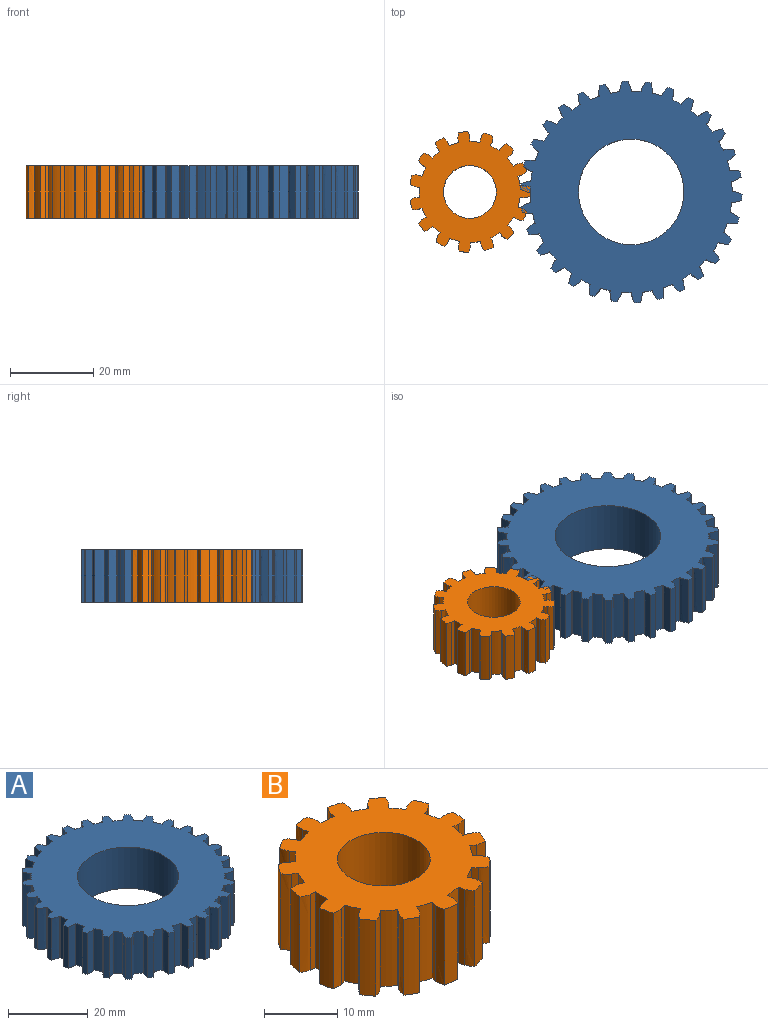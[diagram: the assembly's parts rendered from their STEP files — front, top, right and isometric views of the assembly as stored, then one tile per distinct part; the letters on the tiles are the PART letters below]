
ASSEMBLY  parts=2 mates=1
PART A: 183 faces, bbox 53.4x53.4x12.7 mm
  f0: cylinder r=24.29mm len=12.7mm, axis (0,0,-1), area 30.3mm2, adj f32,f34,f35,f147
  f1: cylinder r=24.29mm len=12.7mm, axis (0,0,-1), area 30.3mm2, adj f34,f35,f142,f146
  f2: cylinder r=24.29mm len=12.7mm, axis (0,0,-1), area 30.3mm2, adj f34,f35,f137,f141
  f3: cylinder r=24.29mm len=12.7mm, axis (0,0,-1), area 30.3mm2, adj f34,f35,f132,f136
  f4: cylinder r=24.29mm len=12.7mm, axis (0,0,-1), area 30.3mm2, adj f34,f35,f127,f131
  f5: cylinder r=24.29mm len=12.7mm, axis (0,0,-1), area 30.3mm2, adj f34,f35,f122,f126
  f6: cylinder r=24.29mm len=12.7mm, axis (0,0,-1), area 30.3mm2, adj f34,f35,f117,f121
  f7: cylinder r=24.29mm len=12.7mm, axis (0,0,-1), area 30.3mm2, adj f34,f35,f112,f116
  f8: cylinder r=24.29mm len=12.7mm, axis (0,0,-1), area 30.3mm2, adj f34,f35,f107,f111
  f9: cylinder r=24.29mm len=12.7mm, axis (0,0,-1), area 30.3mm2, adj f34,f35,f102,f106
  f10: cylinder r=24.29mm len=12.7mm, axis (0,0,-1), area 30.3mm2, adj f34,f35,f97,f101
  f11: cylinder r=24.29mm len=12.7mm, axis (0,0,-1), area 30.3mm2, adj f34,f35,f92,f96
  f12: cylinder r=24.29mm len=12.7mm, axis (0,0,-1), area 30.3mm2, adj f34,f35,f87,f91
  f13: cylinder r=24.29mm len=12.7mm, axis (0,0,-1), area 30.3mm2, adj f34,f35,f82,f86
  f14: cylinder r=24.29mm len=12.7mm, axis (0,0,-1), area 30.3mm2, adj f34,f35,f77,f81
  f15: cylinder r=24.29mm len=12.7mm, axis (0,0,-1), area 30.3mm2, adj f34,f35,f72,f76
  f16: cylinder r=24.29mm len=12.7mm, axis (0,0,-1), area 30.3mm2, adj f34,f35,f67,f71
  f17: cylinder r=24.29mm len=12.7mm, axis (0,0,-1), area 30.3mm2, adj f34,f35,f62,f66
  f18: cylinder r=24.29mm len=12.7mm, axis (0,0,-1), area 30.3mm2, adj f34,f35,f57,f61
  f19: cylinder r=24.29mm len=12.7mm, axis (0,0,-1), area 30.3mm2, adj f34,f35,f52,f56
  f20: cylinder r=24.29mm len=12.7mm, axis (0,0,-1), area 30.3mm2, adj f34,f35,f47,f51
  f21: cylinder r=24.29mm len=12.7mm, axis (0,0,-1), area 30.3mm2, adj f34,f35,f42,f46
  f22: cylinder r=24.29mm len=12.7mm, axis (0,0,-1), area 30.3mm2, adj f34,f35,f41,f182
  f23: cylinder r=24.29mm len=12.7mm, axis (0,0,-1), area 30.3mm2, adj f34,f35,f177,f181
  f24: cylinder r=24.29mm len=12.7mm, axis (0,0,-1), area 30.3mm2, adj f34,f35,f172,f176
  f25: cylinder r=24.29mm len=12.7mm, axis (0,0,-1), area 30.3mm2, adj f34,f35,f167,f171
  f26: cylinder r=24.29mm len=12.7mm, axis (0,0,-1), area 30.3mm2, adj f34,f35,f162,f166
  f27: cylinder r=24.29mm len=12.7mm, axis (0,0,-1), area 30.3mm2, adj f34,f35,f157,f161
  f28: cylinder r=24.29mm len=12.7mm, axis (0,0,-1), area 30.3mm2, adj f34,f35,f151,f156
  f29: extruded ~12.7x2.16mm, area 29.2mm2, adj f30,f33,f34,f35
  f30: cylinder r=26.67mm len=12.7mm, axis (0,0,-1), area 18.2mm2, adj f29,f31,f34,f35
  f31: extruded ~12.7x2.23mm, area 29.2mm2, adj f30,f32,f34,f35
  f32: plane 12.7x0.21mm, normal (-0.99,-0.11,0), area 2.7mm2, adj f0,f31,f34,f35
  f33: plane 12.7x0.21mm, normal (1,0,0), area 2.7mm2, adj f29,f34,f35,f37
  f34: plane 53.37x53.36mm, normal (0,0,1), area 1505.3mm2, adj f0,f1,f2,f3,f4,f5,f6,f7
  f35: plane 53.37x53.36mm, normal (0,0,-1), area 1505.3mm2, adj f0,f1,f2,f3,f4,f5,f6,f7
  f36: cylinder r=12.7mm len=25.4mm, axis (0,0,-1), area 1013.4mm2, adj f34,f35
  f37: cylinder r=24.29mm len=12.7mm, axis (0,0,-1), area 30.3mm2, adj f33,f34,f35,f152
  f38: extruded ~12.7x2.23mm, area 29.2mm2, adj f34,f35,f39,f42
  f39: cylinder r=26.67mm len=12.7mm, axis (0,0,-1), area 18.2mm2, adj f34,f35,f38,f40
  f40: extruded ~12.7x2.17mm, area 29.2mm2, adj f34,f35,f39,f41
  f41: plane 12.7x0.21mm, normal (-0.01,1,0), area 2.7mm2, adj f22,f34,f35,f40
  f42: plane 12.7x0.21mm, normal (-0.1,-0.99,0), area 2.7mm2, adj f21,f34,f35,f38
  f43: extruded ~12.7x2.29mm, area 29.2mm2, adj f34,f35,f44,f47
  f44: cylinder r=26.67mm len=12.7mm, axis (0,0,-1), area 18.2mm2, adj f34,f35,f43,f45
  f45: extruded ~12.7x1.96mm, area 29.2mm2, adj f34,f35,f44,f46
  f46: plane 12.7x0.21mm, normal (0.2,0.98,0), area 2.7mm2, adj f21,f34,f35,f45
  f47: plane 12.7x0.2mm, normal (-0.31,-0.95,0), area 2.7mm2, adj f20,f34,f35,f43
  f48: extruded ~12.7x2.25mm, area 29.2mm2, adj f34,f35,f49,f52
  f49: cylinder r=26.67mm len=12.7mm, axis (0,0,-1), area 18.2mm2, adj f34,f35,f48,f50
  f50: extruded ~12.7x1.67mm, area 29.2mm2, adj f34,f35,f49,f51
  f51: plane 12.7x0.19mm, normal (0.4,0.92,0), area 2.7mm2, adj f20,f34,f35,f50
  f52: plane 12.7x0.18mm, normal (-0.5,-0.87,0), area 2.7mm2, adj f19,f34,f35,f48
  f53: extruded ~12.7x2.12mm, area 29.2mm2, adj f34,f35,f54,f57
  f54: cylinder r=26.67mm len=12.7mm, axis (0,0,-1), area 18.2mm2, adj f34,f35,f53,f55
  f55: extruded ~12.7x1.88mm, area 29.2mm2, adj f34,f35,f54,f56
  f56: plane 12.7x0.17mm, normal (0.58,0.81,0), area 2.7mm2, adj f19,f34,f35,f55
  f57: plane 12.7x0.16mm, normal (-0.67,-0.74,0), area 2.7mm2, adj f18,f34,f35,f53
  f58: extruded ~12.7x1.89mm, area 29.2mm2, adj f34,f35,f59,f62
  f59: cylinder r=26.67mm len=12.7mm, axis (0,0,-1), area 18.2mm2, adj f34,f35,f58,f60
  f60: extruded ~12.7x2.11mm, area 29.2mm2, adj f34,f35,f59,f61
  f61: plane 12.7x0.15mm, normal (0.74,0.67,0), area 2.7mm2, adj f18,f34,f35,f60
  f62: plane 12.7x0.17mm, normal (-0.81,-0.59,0), area 2.7mm2, adj f17,f34,f35,f58
  f63: extruded ~12.7x1.66mm, area 29.2mm2, adj f34,f35,f64,f67
  f64: cylinder r=26.67mm len=12.7mm, axis (0,0,-1), area 18.2mm2, adj f34,f35,f63,f65
  f65: extruded ~12.7x2.25mm, area 29.2mm2, adj f34,f35,f64,f66
  f66: plane 12.7x0.18mm, normal (0.86,0.51,0), area 2.7mm2, adj f17,f34,f35,f65
  f67: plane 12.7x0.19mm, normal (-0.91,-0.41,0), area 2.7mm2, adj f16,f34,f35,f63
  f68: extruded ~12.7x1.95mm, area 29.2mm2, adj f34,f35,f69,f72
  f69: cylinder r=26.67mm len=12.7mm, axis (0,0,-1), area 18.2mm2, adj f34,f35,f68,f70
  f70: extruded ~12.7x2.29mm, area 29.2mm2, adj f34,f35,f69,f71
  f71: plane 12.7x0.2mm, normal (0.95,0.32,0), area 2.7mm2, adj f16,f34,f35,f70
  f72: plane 12.7x0.21mm, normal (-0.98,-0.21,0), area 2.7mm2, adj f15,f34,f35,f68
  f73: extruded ~12.7x2.16mm, area 29.2mm2, adj f34,f35,f74,f77
  f74: cylinder r=26.67mm len=12.7mm, axis (0,0,-1), area 18.2mm2, adj f34,f35,f73,f75
  f75: extruded ~12.7x2.23mm, area 29.2mm2, adj f34,f35,f74,f76
  f76: plane 12.7x0.21mm, normal (0.99,0.11,0), area 2.7mm2, adj f15,f34,f35,f75
  f77: plane 12.7x0.21mm, normal (-1,0,0), area 2.7mm2, adj f14,f34,f35,f73
  f78: extruded ~12.7x2.27mm, area 29.2mm2, adj f34,f35,f79,f82
  f79: cylinder r=26.67mm len=12.7mm, axis (0,0,-1), area 18.2mm2, adj f34,f35,f78,f80
  f80: extruded ~12.7x2.08mm, area 29.2mm2, adj f34,f35,f79,f81
  f81: plane 12.7x0.21mm, normal (1,-0.1,0), area 2.7mm2, adj f14,f34,f35,f80
  f82: plane 12.7x0.21mm, normal (-0.98,0.21,0), area 2.7mm2, adj f13,f34,f35,f78
  f83: extruded ~12.7x2.29mm, area 29.2mm2, adj f34,f35,f84,f87
  f84: cylinder r=26.67mm len=12.7mm, axis (0,0,-1), area 18.2mm2, adj f34,f35,f83,f85
  f85: extruded ~12.7x1.83mm, area 29.2mm2, adj f34,f35,f84,f86
  f86: plane 12.7x0.2mm, normal (0.95,-0.3,0), area 2.7mm2, adj f13,f34,f35,f85
  f87: plane 12.7x0.19mm, normal (-0.91,0.41,0), area 2.7mm2, adj f12,f34,f35,f83
  f88: extruded ~12.7x2.2mm, area 29.2mm2, adj f34,f35,f89,f92
  f89: cylinder r=26.67mm len=12.7mm, axis (0,0,-1), area 18.2mm2, adj f34,f35,f88,f90
  f90: extruded ~12.7x1.73mm, area 29.2mm2, adj f34,f35,f89,f91
  f91: plane 12.7x0.18mm, normal (0.87,-0.49,0), area 2.7mm2, adj f12,f34,f35,f90
  f92: plane 12.7x0.17mm, normal (-0.81,0.59,0), area 2.7mm2, adj f11,f34,f35,f88
  f93: extruded ~12.7x2.02mm, area 29.2mm2, adj f34,f35,f94,f97
  f94: cylinder r=26.67mm len=12.7mm, axis (0,0,-1), area 18.2mm2, adj f34,f35,f93,f95
  f95: extruded ~12.7x2.01mm, area 29.2mm2, adj f34,f35,f94,f96
  f96: plane 12.7x0.16mm, normal (0.75,-0.66,0), area 2.7mm2, adj f11,f34,f35,f95
  f97: plane 12.7x0.16mm, normal (-0.67,0.74,0), area 2.7mm2, adj f10,f34,f35,f93
  f98: extruded ~12.7x1.74mm, area 29.2mm2, adj f34,f35,f99,f102
  f99: cylinder r=26.67mm len=12.7mm, axis (0,0,-1), area 18.2mm2, adj f34,f35,f98,f100
  f100: extruded ~12.7x2.19mm, area 29.2mm2, adj f34,f35,f99,f101
  f101: plane 12.7x0.17mm, normal (0.59,-0.81,0), area 2.7mm2, adj f10,f34,f35,f100
  f102: plane 12.7x0.18mm, normal (-0.5,0.87,0), area 2.7mm2, adj f9,f34,f35,f98
  f103: extruded ~12.7x1.82mm, area 29.2mm2, adj f34,f35,f104,f107
  f104: cylinder r=26.67mm len=12.7mm, axis (0,0,-1), area 18.2mm2, adj f34,f35,f103,f105
  f105: extruded ~12.7x2.28mm, area 29.2mm2, adj f34,f35,f104,f106
  f106: plane 12.7x0.19mm, normal (0.41,-0.91,0), area 2.7mm2, adj f9,f34,f35,f105
  f107: plane 12.7x0.2mm, normal (-0.31,0.95,0), area 2.7mm2, adj f8,f34,f35,f103
  f108: extruded ~12.7x2.07mm, area 29.2mm2, adj f34,f35,f109,f112
  f109: cylinder r=26.67mm len=12.7mm, axis (0,0,-1), area 18.2mm2, adj f34,f35,f108,f110
  f110: extruded ~12.7x2.28mm, area 29.2mm2, adj f34,f35,f109,f111
  f111: plane 12.7x0.2mm, normal (0.21,-0.98,0), area 2.7mm2, adj f8,f34,f35,f110
  f112: plane 12.7x0.21mm, normal (-0.1,0.99,0), area 2.7mm2, adj f7,f34,f35,f108
  f113: extruded ~12.7x2.23mm, area 29.2mm2, adj f34,f35,f114,f117
  f114: cylinder r=26.67mm len=12.7mm, axis (0,0,-1), area 18.2mm2, adj f34,f35,f113,f115
  f115: extruded ~12.7x2.17mm, area 29.2mm2, adj f34,f35,f114,f116
  f116: plane 12.7x0.21mm, normal (0.01,-1,0), area 2.7mm2, adj f7,f34,f35,f115
  f117: plane 12.7x0.21mm, normal (0.1,0.99,0), area 2.7mm2, adj f6,f34,f35,f113
  f118: extruded ~12.7x2.29mm, area 29.2mm2, adj f34,f35,f119,f122
  f119: cylinder r=26.67mm len=12.7mm, axis (0,0,-1), area 18.2mm2, adj f34,f35,f118,f120
  f120: extruded ~12.7x1.96mm, area 29.2mm2, adj f34,f35,f119,f121
  f121: plane 12.7x0.21mm, normal (-0.2,-0.98,0), area 2.7mm2, adj f6,f34,f35,f120
  f122: plane 12.7x0.2mm, normal (0.31,0.95,0), area 2.7mm2, adj f5,f34,f35,f118
  f123: extruded ~12.7x2.25mm, area 29.2mm2, adj f34,f35,f124,f127
  f124: cylinder r=26.67mm len=12.7mm, axis (0,0,-1), area 18.2mm2, adj f34,f35,f123,f125
  f125: extruded ~12.7x1.67mm, area 29.2mm2, adj f34,f35,f124,f126
  f126: plane 12.7x0.19mm, normal (-0.4,-0.92,0), area 2.7mm2, adj f5,f34,f35,f125
  f127: plane 12.7x0.18mm, normal (0.5,0.87,0), area 2.7mm2, adj f4,f34,f35,f123
  f128: extruded ~12.7x2.12mm, area 29.2mm2, adj f34,f35,f129,f132
  f129: cylinder r=26.67mm len=12.7mm, axis (0,0,-1), area 18.2mm2, adj f34,f35,f128,f130
  f130: extruded ~12.7x1.88mm, area 29.2mm2, adj f34,f35,f129,f131
  f131: plane 12.7x0.17mm, normal (-0.58,-0.81,0), area 2.7mm2, adj f4,f34,f35,f130
  f132: plane 12.7x0.16mm, normal (0.67,0.74,0), area 2.7mm2, adj f3,f34,f35,f128
  f133: extruded ~12.7x1.89mm, area 29.2mm2, adj f34,f35,f134,f137
  f134: cylinder r=26.67mm len=12.7mm, axis (0,0,-1), area 18.2mm2, adj f34,f35,f133,f135
  f135: extruded ~12.7x2.11mm, area 29.2mm2, adj f34,f35,f134,f136
  f136: plane 12.7x0.15mm, normal (-0.74,-0.67,0), area 2.7mm2, adj f3,f34,f35,f135
  f137: plane 12.7x0.17mm, normal (0.81,0.59,0), area 2.7mm2, adj f2,f34,f35,f133
  f138: extruded ~12.7x1.66mm, area 29.2mm2, adj f34,f35,f139,f142
  f139: cylinder r=26.67mm len=12.7mm, axis (0,0,-1), area 18.2mm2, adj f34,f35,f138,f140
  f140: extruded ~12.7x2.25mm, area 29.2mm2, adj f34,f35,f139,f141
  f141: plane 12.7x0.18mm, normal (-0.86,-0.51,0), area 2.7mm2, adj f2,f34,f35,f140
  f142: plane 12.7x0.19mm, normal (0.91,0.41,0), area 2.7mm2, adj f1,f34,f35,f138
  f143: extruded ~12.7x1.95mm, area 29.2mm2, adj f34,f35,f144,f147
  f144: cylinder r=26.67mm len=12.7mm, axis (0,0,-1), area 18.2mm2, adj f34,f35,f143,f145
  f145: extruded ~12.7x2.29mm, area 29.2mm2, adj f34,f35,f144,f146
  f146: plane 12.7x0.2mm, normal (-0.95,-0.32,0), area 2.7mm2, adj f1,f34,f35,f145
  f147: plane 12.7x0.21mm, normal (0.98,0.21,0), area 2.7mm2, adj f0,f34,f35,f143
  f148: extruded ~12.7x2.27mm, area 29.2mm2, adj f34,f35,f149,f151
  f149: cylinder r=26.67mm len=12.7mm, axis (0,0,-1), area 18.2mm2, adj f34,f35,f148,f150
  f150: extruded ~12.7x2.08mm, area 29.2mm2, adj f34,f35,f149,f152
  f151: plane 12.7x0.21mm, normal (0.98,-0.21,0), area 2.7mm2, adj f28,f34,f35,f148
  f152: plane 12.7x0.21mm, normal (-1,0.1,0), area 2.7mm2, adj f34,f35,f37,f150
  f153: extruded ~12.7x2.29mm, area 29.2mm2, adj f34,f35,f154,f157
  f154: cylinder r=26.67mm len=12.7mm, axis (0,0,-1), area 18.2mm2, adj f34,f35,f153,f155
  f155: extruded ~12.7x1.83mm, area 29.2mm2, adj f34,f35,f154,f156
  f156: plane 12.7x0.2mm, normal (-0.95,0.3,0), area 2.7mm2, adj f28,f34,f35,f155
  f157: plane 12.7x0.19mm, normal (0.91,-0.41,0), area 2.7mm2, adj f27,f34,f35,f153
  f158: extruded ~12.7x2.2mm, area 29.2mm2, adj f34,f35,f159,f162
  f159: cylinder r=26.67mm len=12.7mm, axis (0,0,-1), area 18.2mm2, adj f34,f35,f158,f160
  f160: extruded ~12.7x1.73mm, area 29.2mm2, adj f34,f35,f159,f161
  f161: plane 12.7x0.18mm, normal (-0.87,0.49,0), area 2.7mm2, adj f27,f34,f35,f160
  f162: plane 12.7x0.17mm, normal (0.81,-0.59,0), area 2.7mm2, adj f26,f34,f35,f158
  f163: extruded ~12.7x2.02mm, area 29.2mm2, adj f34,f35,f164,f167
  f164: cylinder r=26.67mm len=12.7mm, axis (0,0,-1), area 18.2mm2, adj f34,f35,f163,f165
  f165: extruded ~12.7x2.01mm, area 29.2mm2, adj f34,f35,f164,f166
  f166: plane 12.7x0.16mm, normal (-0.75,0.66,0), area 2.7mm2, adj f26,f34,f35,f165
  f167: plane 12.7x0.16mm, normal (0.67,-0.74,0), area 2.7mm2, adj f25,f34,f35,f163
  f168: extruded ~12.7x1.74mm, area 29.2mm2, adj f34,f35,f169,f172
  f169: cylinder r=26.67mm len=12.7mm, axis (0,0,-1), area 18.2mm2, adj f34,f35,f168,f170
  f170: extruded ~12.7x2.19mm, area 29.2mm2, adj f34,f35,f169,f171
  f171: plane 12.7x0.17mm, normal (-0.59,0.81,0), area 2.7mm2, adj f25,f34,f35,f170
  f172: plane 12.7x0.18mm, normal (0.5,-0.87,0), area 2.7mm2, adj f24,f34,f35,f168
  f173: extruded ~12.7x1.82mm, area 29.2mm2, adj f34,f35,f174,f177
  f174: cylinder r=26.67mm len=12.7mm, axis (0,0,-1), area 18.2mm2, adj f34,f35,f173,f175
  f175: extruded ~12.7x2.28mm, area 29.2mm2, adj f34,f35,f174,f176
  f176: plane 12.7x0.19mm, normal (-0.41,0.91,0), area 2.7mm2, adj f24,f34,f35,f175
  f177: plane 12.7x0.2mm, normal (0.31,-0.95,0), area 2.7mm2, adj f23,f34,f35,f173
  f178: extruded ~12.7x2.07mm, area 29.2mm2, adj f34,f35,f179,f182
  f179: cylinder r=26.67mm len=12.7mm, axis (0,0,-1), area 18.2mm2, adj f34,f35,f178,f180
  f180: extruded ~12.7x2.28mm, area 29.2mm2, adj f34,f35,f179,f181
  f181: plane 12.7x0.2mm, normal (-0.21,0.98,0), area 2.7mm2, adj f23,f34,f35,f180
  f182: plane 12.7x0.21mm, normal (0.1,-0.99,0), area 2.7mm2, adj f22,f34,f35,f178
PART B: 93 faces, bbox 29x29.1x12.7 mm
  f0: cylinder r=12.15mm len=12.7mm, axis (0,0,-1), area 30.5mm2, adj f16,f17,f22,f88
  f1: cylinder r=12.15mm len=12.7mm, axis (0,0,-1), area 30.5mm2, adj f16,f17,f83,f92
  f2: cylinder r=12.15mm len=12.7mm, axis (0,0,-1), area 30.5mm2, adj f16,f17,f78,f87
  f3: cylinder r=12.15mm len=12.7mm, axis (0,0,-1), area 30.5mm2, adj f16,f17,f73,f82
  f4: cylinder r=12.15mm len=12.7mm, axis (0,0,-1), area 30.5mm2, adj f16,f17,f68,f77
  f5: cylinder r=12.15mm len=12.7mm, axis (0,0,-1), area 30.5mm2, adj f16,f17,f63,f72
  f6: cylinder r=12.15mm len=12.7mm, axis (0,0,-1), area 30.5mm2, adj f16,f17,f58,f67
  f7: cylinder r=12.15mm len=12.7mm, axis (0,0,-1), area 30.5mm2, adj f16,f17,f53,f62
  f8: cylinder r=12.15mm len=12.7mm, axis (0,0,-1), area 30.5mm2, adj f16,f17,f48,f57
  f9: cylinder r=12.15mm len=12.7mm, axis (0,0,-1), area 30.5mm2, adj f16,f17,f43,f52
  f10: cylinder r=12.15mm len=12.7mm, axis (0,0,-1), area 30.5mm2, adj f16,f17,f38,f47
  f11: cylinder r=12.15mm len=12.7mm, axis (0,0,-1), area 30.5mm2, adj f16,f17,f33,f42
  f12: cylinder r=12.15mm len=12.7mm, axis (0,0,-1), area 30.5mm2, adj f16,f17,f28,f37
  f13: cylinder r=12.15mm len=12.7mm, axis (0,0,-1), area 30.5mm2, adj f16,f17,f23,f32
  f14: cylinder r=12.15mm len=12.7mm, axis (0,0,-1), area 30.5mm2, adj f16,f17,f18,f27
  f15: cylinder r=6.35mm len=12.7mm, axis (0,0,-1), area 506.7mm2, adj f16,f17
  f16: plane 29.07x28.96mm, normal (0,0,1), area 433.6mm2, adj f0,f1,f2,f3,f4,f5,f6,f7
  f17: plane 29.07x28.96mm, normal (0,0,-1), area 433.6mm2, adj f0,f1,f2,f3,f4,f5,f6,f7
  f18: plane 12.7x0.94mm, normal (1,0,0), area 12mm2, adj f14,f16,f17,f19
  f19: extruded ~12.7x1.43mm, area 19.3mm2, adj f16,f17,f18,f20
  f20: cylinder r=14.53mm len=12.7mm, axis (0,0,-1), area 28.4mm2, adj f16,f17,f19,f21
  f21: extruded ~12.7x1.5mm, area 19.3mm2, adj f16,f17,f20,f22
  f22: plane 12.7x0.92mm, normal (-0.98,-0.22,0), area 12mm2, adj f0,f16,f17,f21
  f23: plane 12.7x0.86mm, normal (0.91,-0.41,0), area 12mm2, adj f13,f16,f17,f24
  f24: extruded ~12.7x1.5mm, area 19.3mm2, adj f16,f17,f23,f25
  f25: cylinder r=14.53mm len=12.7mm, axis (0,0,-1), area 28.4mm2, adj f16,f17,f24,f26
  f26: extruded ~12.7x1.31mm, area 19.3mm2, adj f16,f17,f25,f27
  f27: plane 12.7x0.93mm, normal (-0.98,0.2,0), area 12mm2, adj f14,f16,f17,f26
  f28: plane 12.7x0.7mm, normal (0.67,-0.74,0), area 12mm2, adj f12,f16,f17,f29
  f29: extruded ~12.7x1.32mm, area 19.3mm2, adj f16,f17,f28,f30
  f30: cylinder r=14.53mm len=12.7mm, axis (0,0,-1), area 28.4mm2, adj f16,f17,f29,f31
  f31: extruded ~12.7x1.22mm, area 19.3mm2, adj f16,f17,f30,f32
  f32: plane 12.7x0.77mm, normal (-0.82,0.58,0), area 12mm2, adj f13,f16,f17,f31
  f33: plane 12.7x0.9mm, normal (0.31,-0.95,0), area 12mm2, adj f11,f16,f17,f34
  f34: extruded ~12.7x1.21mm, area 19.3mm2, adj f16,f17,f33,f35
  f35: cylinder r=14.53mm len=12.7mm, axis (0,0,-1), area 28.4mm2, adj f16,f17,f34,f36
  f36: extruded ~12.7x1.48mm, area 19.3mm2, adj f16,f17,f35,f37
  f37: plane 12.7x0.81mm, normal (-0.51,0.86,0), area 12mm2, adj f12,f16,f17,f36
  f38: plane 12.7x0.94mm, normal (-0.1,-0.99,0), area 12mm2, adj f10,f16,f17,f39
  f39: extruded ~12.7x1.47mm, area 19.3mm2, adj f16,f17,f38,f40
  f40: cylinder r=14.53mm len=12.7mm, axis (0,0,-1), area 28.4mm2, adj f16,f17,f39,f41
  f41: extruded ~12.7x1.48mm, area 19.3mm2, adj f16,f17,f40,f42
  f42: plane 12.7x0.94mm, normal (-0.12,0.99,0), area 12mm2, adj f11,f16,f17,f41
  f43: plane 12.7x0.82mm, normal (-0.5,-0.87,0), area 12mm2, adj f9,f16,f17,f44
  f44: extruded ~12.7x1.48mm, area 19.3mm2, adj f16,f17,f43,f45
  f45: cylinder r=14.53mm len=12.7mm, axis (0,0,-1), area 28.4mm2, adj f16,f17,f44,f46
  f46: extruded ~12.7x1.22mm, area 19.3mm2, adj f16,f17,f45,f47
  f47: plane 12.7x0.9mm, normal (0.3,0.95,0), area 12mm2, adj f10,f16,f17,f46
  f48: plane 12.7x0.76mm, normal (-0.81,-0.59,0), area 12mm2, adj f8,f16,f17,f49
  f49: extruded ~12.7x1.23mm, area 19.3mm2, adj f16,f17,f48,f50
  f50: cylinder r=14.53mm len=12.7mm, axis (0,0,-1), area 28.4mm2, adj f16,f17,f49,f51
  f51: extruded ~12.7x1.31mm, area 19.3mm2, adj f16,f17,f50,f52
  f52: plane 12.7x0.71mm, normal (0.66,0.75,0), area 12mm2, adj f9,f16,f17,f51
  f53: plane 12.7x0.92mm, normal (-0.98,-0.21,0), area 12mm2, adj f7,f16,f17,f54
  f54: extruded ~12.7x1.3mm, area 19.3mm2, adj f16,f17,f53,f55
  f55: cylinder r=14.53mm len=12.7mm, axis (0,0,-1), area 28.4mm2, adj f16,f17,f54,f56
  f56: extruded ~12.7x1.5mm, area 19.3mm2, adj f16,f17,f55,f57
  f57: plane 12.7x0.86mm, normal (0.91,0.42,0), area 12mm2, adj f8,f16,f17,f56
  f58: plane 12.7x0.92mm, normal (-0.98,0.21,0), area 12mm2, adj f6,f16,f17,f59
  f59: extruded ~12.7x1.5mm, area 19.3mm2, adj f16,f17,f58,f60
  f60: cylinder r=14.53mm len=12.7mm, axis (0,0,-1), area 28.4mm2, adj f16,f17,f59,f61
  f61: extruded ~12.7x1.44mm, area 19.3mm2, adj f16,f17,f60,f62
  f62: plane 12.7x0.94mm, normal (1,0.01,0), area 12mm2, adj f7,f16,f17,f61
  f63: plane 12.7x0.76mm, normal (-0.81,0.59,0), area 12mm2, adj f5,f16,f17,f64
  f64: extruded ~12.7x1.44mm, area 19.3mm2, adj f16,f17,f63,f65
  f65: cylinder r=14.53mm len=12.7mm, axis (0,0,-1), area 28.4mm2, adj f16,f17,f64,f66
  f66: extruded ~12.7x1.12mm, area 19.3mm2, adj f16,f17,f65,f67
  f67: plane 12.7x0.87mm, normal (0.92,-0.4,0), area 12mm2, adj f6,f16,f17,f66
  f68: plane 12.7x0.82mm, normal (-0.5,0.87,0), area 12mm2, adj f4,f16,f17,f69
  f69: extruded ~12.7x1.14mm, area 19.3mm2, adj f16,f17,f68,f70
  f70: cylinder r=14.53mm len=12.7mm, axis (0,0,-1), area 28.4mm2, adj f16,f17,f69,f71
  f71: extruded ~12.7x1.38mm, area 19.3mm2, adj f16,f17,f70,f72
  f72: plane 12.7x0.69mm, normal (0.68,-0.74,0), area 12mm2, adj f5,f16,f17,f71
  f73: plane 12.7x0.94mm, normal (-0.1,0.99,0), area 12mm2, adj f3,f16,f17,f74
  f74: extruded ~12.7x1.37mm, area 19.3mm2, adj f16,f17,f73,f75
  f75: cylinder r=14.53mm len=12.7mm, axis (0,0,-1), area 28.4mm2, adj f16,f17,f74,f76
  f76: extruded ~12.7x1.51mm, area 19.3mm2, adj f16,f17,f75,f77
  f77: plane 12.7x0.89mm, normal (0.32,-0.95,0), area 12mm2, adj f4,f16,f17,f76
  f78: plane 12.7x0.9mm, normal (0.31,0.95,0), area 12mm2, adj f2,f16,f17,f79
  f79: extruded ~12.7x1.51mm, area 19.3mm2, adj f16,f17,f78,f80
  f80: cylinder r=14.53mm len=12.7mm, axis (0,0,-1), area 28.4mm2, adj f16,f17,f79,f81
  f81: extruded ~12.7x1.38mm, area 19.3mm2, adj f16,f17,f80,f82
  f82: plane 12.7x0.94mm, normal (-0.09,-1,0), area 12mm2, adj f3,f16,f17,f81
  f83: plane 12.7x0.7mm, normal (0.67,0.74,0), area 12mm2, adj f1,f16,f17,f84
  f84: extruded ~12.7x1.39mm, area 19.3mm2, adj f16,f17,f83,f85
  f85: cylinder r=14.53mm len=12.7mm, axis (0,0,-1), area 28.4mm2, adj f16,f17,f84,f86
  f86: extruded ~12.7x1.13mm, area 19.3mm2, adj f16,f17,f85,f87
  f87: plane 12.7x0.82mm, normal (-0.49,-0.87,0), area 12mm2, adj f2,f16,f17,f86
  f88: plane 12.7x0.86mm, normal (0.91,0.41,0), area 12mm2, adj f0,f16,f17,f89
  f89: extruded ~12.7x1.11mm, area 19.3mm2, adj f16,f17,f88,f90
  f90: cylinder r=14.53mm len=12.7mm, axis (0,0,-1), area 28.4mm2, adj f16,f17,f89,f91
  f91: extruded ~12.7x1.44mm, area 19.3mm2, adj f16,f17,f90,f92
  f92: plane 12.7x0.76mm, normal (-0.8,-0.6,0), area 12mm2, adj f1,f16,f17,f91
PLACE A at identity fixed
PLACE B t=(-38.81,0,0)mm
MATE fastened A.f0 <-> B.f17  axis (0,0,-1) through (0,0,0)mm
